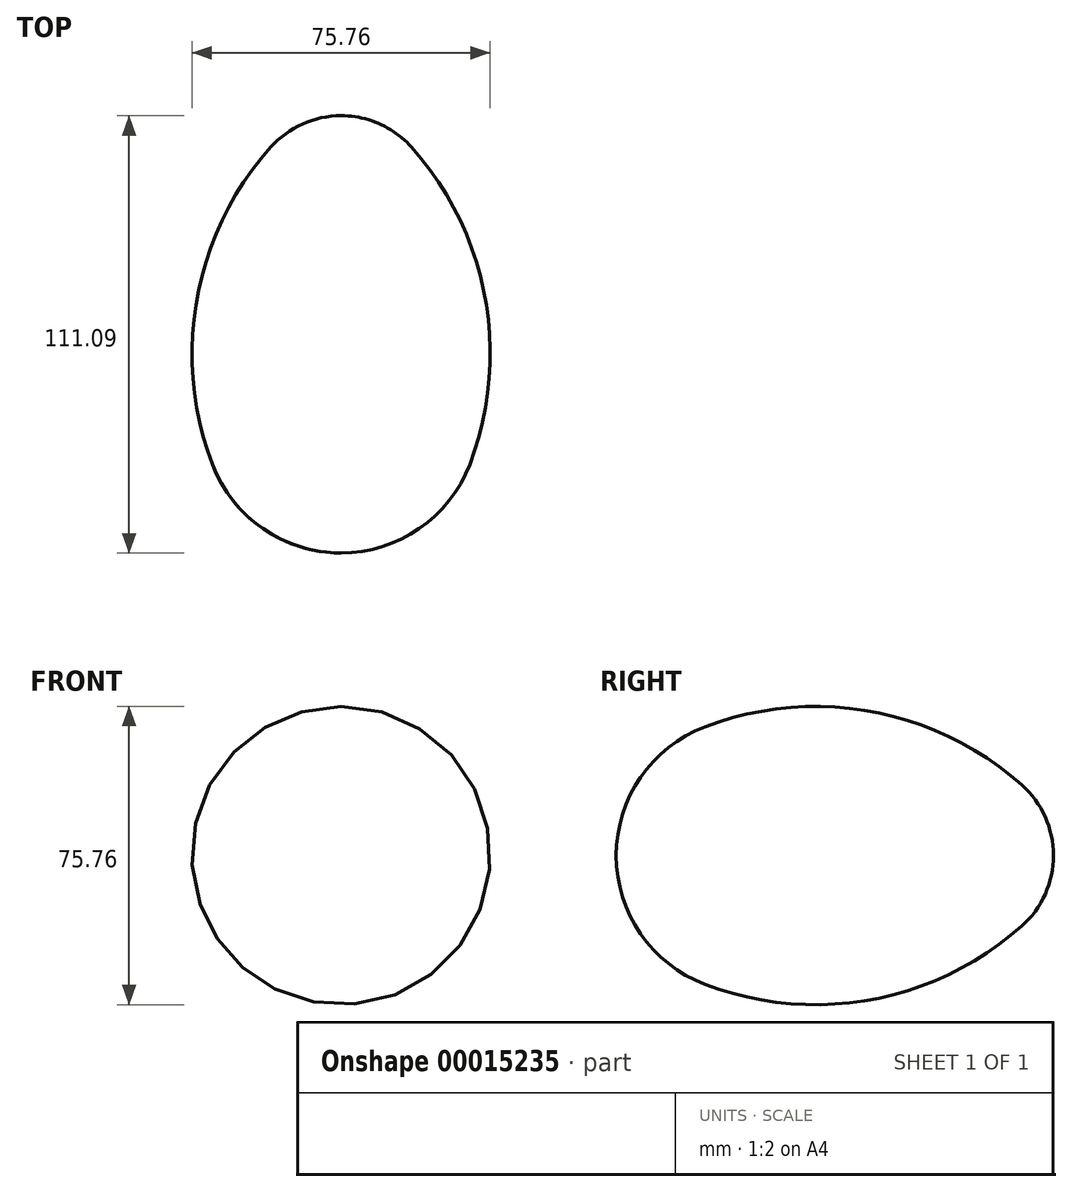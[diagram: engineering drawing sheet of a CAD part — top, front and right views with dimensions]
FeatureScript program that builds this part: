
annotation { "Feature Type Name" : "Feature", "Feature Type Description" : "" }
export const myFeature = defineFeature(function(context is Context, id is Id, definition is map)
    precondition{}
    {
        {
            var Q0;
            Q0=qCreatedBy(makeId("Top.planeOp"),FACE);
            var sketch = newSketch(context, id + "F0", { "sketchPlane" : qUnion([Q0])});
            skArc(sketch, "E0", {"start": v(-32.7, -64.58) * mm, "mid": v(-19.86, -80.93) * mm, "end": v(0, -87.11) * mm});
            skArc(sketch, "E1", {"start": v(0, 23.98) * mm, "mid": v(-9.81, 21.88) * mm, "end": v(-17.9, 15.95) * mm});
            skArc(sketch, "E2", {"start": v(-17.9, 15.95) * mm, "mid": v(-36.58, -22.24) * mm, "end": v(-32.7, -64.58) * mm});
            skLineSegment(sketch, "E3", {"start": v(0, 23.98) * mm, "end": v(0, -87.11) * mm});
            skPoint(sketch, "E4.MirrorCS.end.orphan", {"position": v(32.7, -64.58) * mm});
            skPoint(sketch, "E5.orphan", {"position": v(17.9, 15.95) * mm});
            skPoint(sketch, "E6.orphan", {"position": v(0, 58.06) * mm});
            skSolve(sketch);
        }
        {
            var Q0;
            Q0=makeQuery(id+"F0.imprint","IMPRINT",FACE,{"disambiguationData":[TD([[makeQuery(id+"F0.imprint","IMPRINT",EDGE,{"derivedFrom":sQuery(id+"F0.wireOp",EDGE,"E0")}),1.0]])]});
            var Q1;
            Q1=sQuery(id+"F0.wireOp",EDGE,"E3");
            revolve(context, id + "F1", {"entities" : qUnion([Q0]), "axis" : qUnion([Q1]), "revolveType" : RevolveType.FULL});
        }
        {
            var Q0;
            Q0=makeQuery(id+"F1.opRevolve","SWEPT_BODY",BODY,{"disambiguationData":[OSD([sQuery(id+"F0.wireOp",EDGE,"E0"),sQuery(id+"F0.wireOp",EDGE,"E1"),sQuery(id+"F0.wireOp",EDGE,"E2"),sQuery(id+"F0.wireOp",EDGE,"E3")])]});
            transform(context, id + "F2", {"entities" : qUnion([Q0]), "transformType" : TransformType.TRANSLATION_3D, "dx" : 0 * mm, "dy" : 30.12 * mm, "dz" : 0 * mm, "makeCopy" : false});
        }
    });
